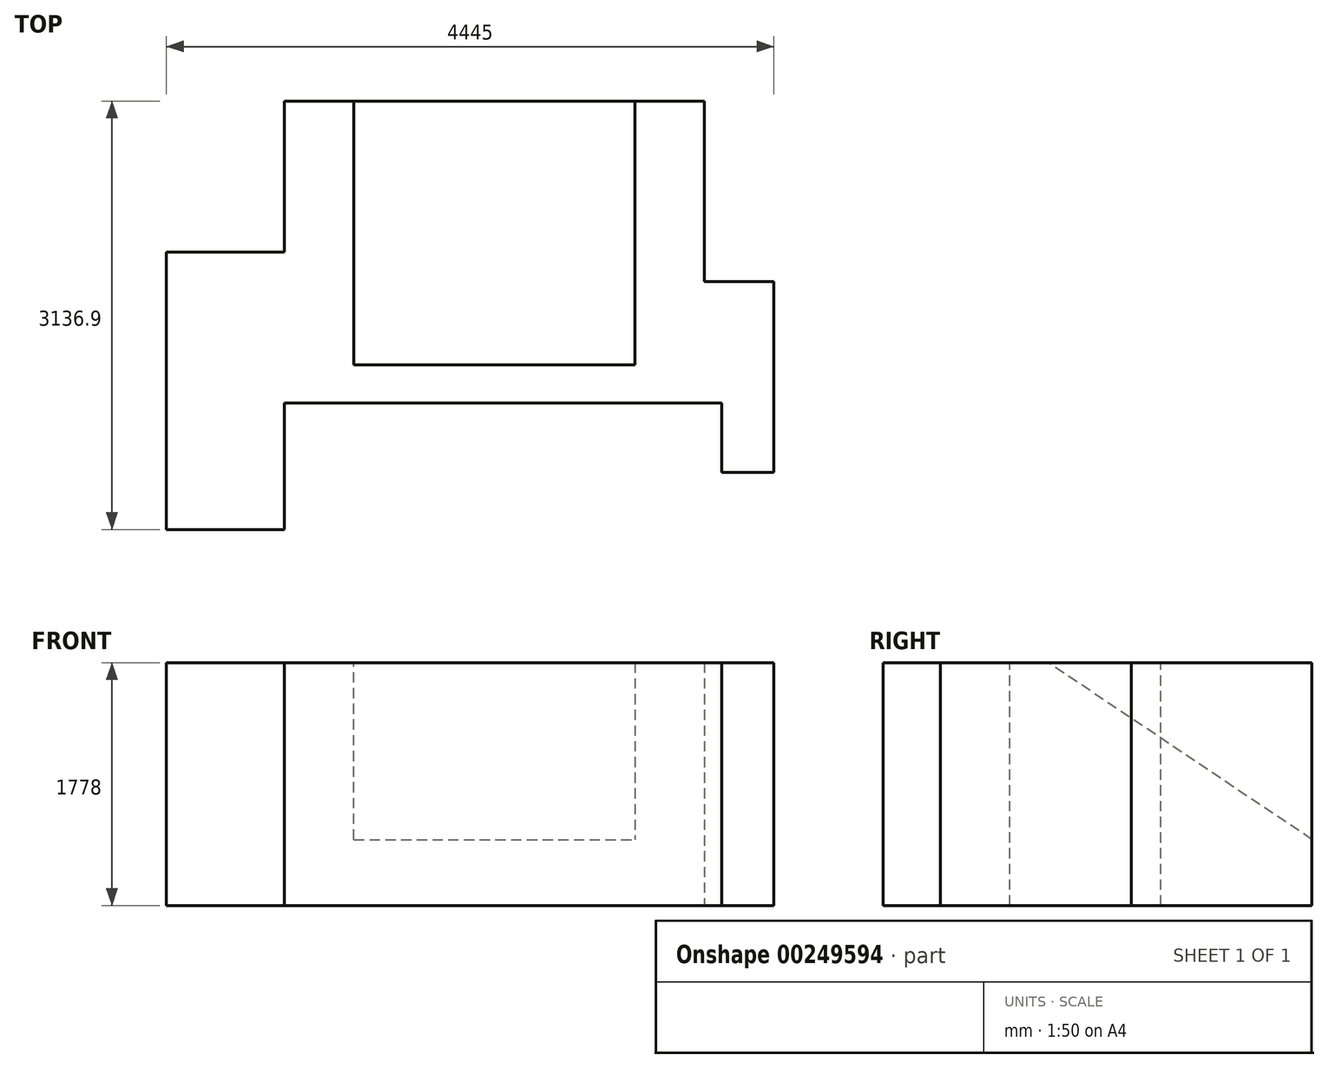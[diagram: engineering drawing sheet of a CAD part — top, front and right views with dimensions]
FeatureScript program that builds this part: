
annotation { "Feature Type Name" : "Feature", "Feature Type Description" : "" }
export const myFeature = defineFeature(function(context is Context, id is Id, definition is map)
    precondition{}
    {
        {
            var Q0;
            Q0=qCreatedBy(makeId("Top.planeOp"),FACE);
            var sketch = newSketch(context, id + "F0", { "sketchPlane" : qUnion([Q0])});
            skLineSegment(sketch, "E0.bottom", {"start": v(0, 0) * mm, "end": v(2057.4, 0) * mm});
            skLineSegment(sketch, "E0.top", {"start": v(0, 1930.4) * mm, "end": v(2057.4, 1930.4) * mm});
            skLineSegment(sketch, "E0.left", {"start": v(0, 0) * mm, "end": v(0, 1930.4) * mm});
            skLineSegment(sketch, "E0.right", {"start": v(2057.4, 0) * mm, "end": v(2057.4, 1930.4) * mm});
            skSolve(sketch);
        }
        {
            var Q0;
            Q0=makeQuery(id+"F0.imprint","IMPRINT",FACE,{"disambiguationData":[TD([[makeQuery(id+"F0.imprint","IMPRINT",EDGE,{"derivedFrom":sQuery(id+"F0.wireOp",EDGE,"E0.bottom")}),1.0]])]});
            extrude(context, id + "F1", {"entities" : qUnion([Q0]), "depth" : 1295.4 * mm});
        }
        {
            var Q0;
            Q0=makeQuery(id+"F1.opExtrude","CAP_EDGE",EDGE,{"disambiguationData":[OSD([sQuery(id+"F0.wireOp",EDGE,"E0.top")])],"isStart":false});
            chamfer(context, id + "F2", {"entities" : qUnion([Q0]), "chamferType" : ChamferType.TWO_OFFSETS, "width1" : 1295.4 * mm, "oppositeDirection" : false, "width2" : 1930.4 * mm, "tangentPropagation" : true});
        }
        {
            var Q0;
            Q0=makeQuery(id+"F1.opExtrude","SWEPT_FACE",FACE,{"disambiguationData":[OSD([sQuery(id+"F0.wireOp",EDGE,"E0.left")])]});
            var sketch = newSketch(context, id + "F3", { "sketchPlane" : qUnion([Q0])});
            skLineSegment(sketch, "E1.bottom", {"start": v(0, 0) * mm, "end": v(-1930.4, 0) * mm});
            skLineSegment(sketch, "E1.top", {"start": v(0, 1295.4) * mm, "end": v(-1930.4, 1295.4) * mm});
            skLineSegment(sketch, "E1.left", {"start": v(0, 0) * mm, "end": v(0, 1295.4) * mm});
            skLineSegment(sketch, "E1.right", {"start": v(-1930.4, 0) * mm, "end": v(-1930.4, 1295.4) * mm});
            skSolve(sketch);
        }
        {
            var Q0;
            Q0=makeQuery(id+"F3.imprint","IMPRINT",FACE,{"disambiguationData":[TD([[makeQuery(id+"F3.imprint","IMPRINT",EDGE,{"derivedFrom":sQuery(id+"F3.wireOp",EDGE,"E1.top")}),1.0]])]});
            var Q1;
            Q1=makeQuery(id+"F3.imprint","IMPRINT",FACE,{"disambiguationData":[TD([[makeQuery(id+"F3.imprint","IMPRINT",EDGE,{"derivedFrom":sQuery(id+"F3.wireOp",EDGE,"E1.bottom")}),-1.0]])]});
            extrude(context, id + "F4", {"entities" : qUnion([Q0, Q1]), "operationType" : NewBodyOperationType.ADD, "depth" : 508 * mm});
        }
        {
            var Q0;
            Q0=makeQuery(id+"F1.opExtrude","SWEPT_FACE",FACE,{"disambiguationData":[OSD([sQuery(id+"F0.wireOp",EDGE,"E0.right")])]});
            var sketch = newSketch(context, id + "F5", { "sketchPlane" : qUnion([Q0])});
            skLineSegment(sketch, "E2.0", {"start": v(0, 1295.4) * mm, "end": v(1930.4, 1295.4) * mm});
            skLineSegment(sketch, "E3.0", {"start": v(1930.4, 0) * mm, "end": v(1930.4, 1295.4) * mm});
            skLineSegment(sketch, "E4.top", {"start": v(0, 0) * mm, "end": v(1930.4, 0) * mm});
            skLineSegment(sketch, "E4.left", {"start": v(0, 1295.4) * mm, "end": v(0, 0) * mm});
            skLineSegment(sketch, "E4.right", {"start": v(1930.4, 1295.4) * mm, "end": v(1930.4, 0) * mm});
            skSolve(sketch);
        }
        {
            var Q0;
            Q0=makeQuery(id+"F5.imprint","IMPRINT",FACE,{"disambiguationData":[TD([[makeQuery(id+"F5.imprint","IMPRINT",EDGE,{"derivedFrom":sQuery(id+"F5.wireOp",EDGE,"E2.0")}),-1.0]])]});
            var Q1;
            Q1=makeQuery(id+"F5.imprint","IMPRINT",FACE,{"disambiguationData":[TD([[makeQuery(id+"F5.imprint","IMPRINT",EDGE,{"derivedFrom":sQuery(id+"F5.wireOp",EDGE,"E4.top")}),1.0]])]});
            extrude(context, id + "F6", {"entities" : qUnion([Q0, Q1]), "operationType" : NewBodyOperationType.ADD, "depth" : 508 * mm});
        }
        {
            var Q0;
            Q0=makeQuery(id+"F6.boolean.opBoolean","MERGE",FACE,{"derivedFrom":[makeQuery(id+"F4.boolean.opBoolean","MERGE",FACE,{"derivedFrom":[makeQuery(id+"F1.opExtrude","CAP_FACE",FACE,{"disambiguationData":[OSD([sQuery(id+"F0.wireOp",EDGE,"E0.bottom"),sQuery(id+"F0.wireOp",EDGE,"E0.top"),sQuery(id+"F0.wireOp",EDGE,"E0.left"),sQuery(id+"F0.wireOp",EDGE,"E0.right")])],"isStart":true}),makeQuery(id+"F4.opExtrude","SWEPT_FACE",FACE,{"disambiguationData":[OSD([sQuery(id+"F3.wireOp",EDGE,"E1.bottom")])]})]}),makeQuery(id+"F6.opExtrude","SWEPT_FACE",FACE,{"disambiguationData":[OSD([sQuery(id+"F5.wireOp",EDGE,"E4.top")])]})]});
            var sketch = newSketch(context, id + "F7", { "sketchPlane" : qUnion([Q0])});
            skLineSegment(sketch, "E5.bottom", {"start": v(-508, -1930.4) * mm, "end": v(2565.4, -1930.4) * mm});
            skLineSegment(sketch, "E5.top", {"start": v(-508, 0) * mm, "end": v(2565.4, 0) * mm});
            skLineSegment(sketch, "E5.left", {"start": v(-508, -1930.4) * mm, "end": v(-508, 0) * mm});
            skLineSegment(sketch, "E5.right", {"start": v(2565.4, -1930.4) * mm, "end": v(2565.4, 0) * mm});
            skSolve(sketch);
        }
        {
            var Q0;
            Q0=makeQuery(id+"F7.imprint","IMPRINT",FACE,{"disambiguationData":[TD([[makeQuery(id+"F7.imprint","IMPRINT",EDGE,{"derivedFrom":sQuery(id+"F7.wireOp",EDGE,"E5.top")}),-1.0]])]});
            extrude(context, id + "F8", {"entities" : qUnion([Q0]), "operationType" : NewBodyOperationType.ADD, "depth" : 482.6 * mm});
        }
        {
            var Q0;
            Q0=makeQuery(id+"F8.boolean.opBoolean","MERGE",FACE,{"derivedFrom":[makeQuery(id+"F6.boolean.opBoolean","MERGE",FACE,{"derivedFrom":[makeQuery(id+"F4.boolean.opBoolean","MERGE",FACE,{"derivedFrom":[makeQuery(id+"F1.opExtrude","SWEPT_FACE",FACE,{"disambiguationData":[OSD([sQuery(id+"F0.wireOp",EDGE,"E0.bottom")])]}),makeQuery(id+"F4.opExtrude","SWEPT_FACE",FACE,{"disambiguationData":[OSD([sQuery(id+"F3.wireOp",EDGE,"E1.left")])]})]}),makeQuery(id+"F6.opExtrude","SWEPT_FACE",FACE,{"disambiguationData":[OSD([sQuery(id+"F5.wireOp",EDGE,"E4.left")])]})]}),makeQuery(id+"F8.opExtrude","SWEPT_FACE",FACE,{"disambiguationData":[OSD([sQuery(id+"F7.wireOp",EDGE,"E5.top")])]})]});
            var sketch = newSketch(context, id + "F9", { "sketchPlane" : qUnion([Q0])});
            skLineSegment(sketch, "E6.bottom", {"start": v(-508, -482.6) * mm, "end": v(2565.4, -482.6) * mm});
            skLineSegment(sketch, "E6.top", {"start": v(-508, 1295.4) * mm, "end": v(2565.4, 1295.4) * mm});
            skLineSegment(sketch, "E6.left", {"start": v(-508, -482.6) * mm, "end": v(-508, 1295.4) * mm});
            skLineSegment(sketch, "E6.right", {"start": v(2565.4, -482.6) * mm, "end": v(2565.4, 1295.4) * mm});
            skSolve(sketch);
        }
        {
            var Q0;
            Q0=makeQuery(id+"F9.imprint","IMPRINT",FACE,{"disambiguationData":[TD([[makeQuery(id+"F9.imprint","IMPRINT",EDGE,{"derivedFrom":sQuery(id+"F9.wireOp",EDGE,"E6.bottom")}),1.0]])]});
            extrude(context, id + "F10", {"entities" : qUnion([Q0]), "operationType" : NewBodyOperationType.ADD, "depth" : 279.4 * mm});
        }
        {
            var Q0;
            Q0=makeQuery(id+"F10.boolean.opBoolean","MERGE",FACE,{"derivedFrom":[makeQuery(id+"F8.boolean.opBoolean","MERGE",FACE,{"derivedFrom":[makeQuery(id+"F4.opExtrude","CAP_FACE",FACE,{"disambiguationData":[OSD([sQuery(id+"F3.wireOp",EDGE,"E1.bottom"),sQuery(id+"F3.wireOp",EDGE,"E1.top"),sQuery(id+"F3.wireOp",EDGE,"E1.left"),sQuery(id+"F3.wireOp",EDGE,"E1.right")])],"isStart":false}),makeQuery(id+"F8.opExtrude","SWEPT_FACE",FACE,{"disambiguationData":[OSD([sQuery(id+"F7.wireOp",EDGE,"E5.left")])]})]}),makeQuery(id+"F10.opExtrude","SWEPT_FACE",FACE,{"disambiguationData":[OSD([sQuery(id+"F9.wireOp",EDGE,"E6.left")])]})]});
            var sketch = newSketch(context, id + "F11", { "sketchPlane" : qUnion([Q0])});
            skLineSegment(sketch, "E7.bottom", {"start": v(-1930.4, -482.6) * mm, "end": v(-825.5, -482.6) * mm});
            skLineSegment(sketch, "E7.top", {"start": v(-1930.4, 1295.4) * mm, "end": v(-825.5, 1295.4) * mm});
            skLineSegment(sketch, "E7.left", {"start": v(-1930.4, -482.6) * mm, "end": v(-1930.4, 1295.4) * mm});
            skLineSegment(sketch, "E7.right", {"start": v(-825.5, -482.6) * mm, "end": v(-825.5, 1295.4) * mm});
            skLineSegment(sketch, "E8.bottom", {"start": v(-825.5, -482.6) * mm, "end": v(1206.5, -482.6) * mm});
            skLineSegment(sketch, "E8.top", {"start": v(-825.5, 1295.4) * mm, "end": v(1206.5, 1295.4) * mm});
            skLineSegment(sketch, "E8.right", {"start": v(1206.5, -482.6) * mm, "end": v(1206.5, 1295.4) * mm});
            skSolve(sketch);
        }
        {
            var Q0;
            {var subQ2=sQuery(id+"F11.wireOp",EDGE,"E8.right");Q0=makeQuery(id+"F11.imprint","IMPRINT",FACE,{"disambiguationData":[TD([[makeQuery(id+"F11.imprint","IMPRINT",EDGE,{"derivedFrom":subQ2}),1.0]])]});}
            var Q1;
            {var subQ2=sQuery(id+"F11.wireOp",EDGE,"E7.right");Q1=makeQuery(id+"F11.imprint","IMPRINT",FACE,{"disambiguationData":[TD([[makeQuery(id+"F11.imprint","IMPRINT",EDGE,{"derivedFrom":subQ2}),-1.0]])]});}
            extrude(context, id + "F12", {"entities" : qUnion([Q0, Q1]), "operationType" : NewBodyOperationType.ADD, "depth" : 863.6 * mm});
        }
        {
            var Q0;
            Q0=makeQuery(id+"F10.boolean.opBoolean","MERGE",FACE,{"derivedFrom":[makeQuery(id+"F8.boolean.opBoolean","MERGE",FACE,{"derivedFrom":[makeQuery(id+"F6.opExtrude","CAP_FACE",FACE,{"disambiguationData":[OSD([sQuery(id+"F5.wireOp",EDGE,"E2.0"),sQuery(id+"F5.wireOp",EDGE,"E4.top"),sQuery(id+"F5.wireOp",EDGE,"E4.left"),sQuery(id+"F5.wireOp",EDGE,"E4.right")])],"isStart":false}),makeQuery(id+"F8.opExtrude","SWEPT_FACE",FACE,{"disambiguationData":[OSD([sQuery(id+"F7.wireOp",EDGE,"E5.right")])]})]}),makeQuery(id+"F10.opExtrude","SWEPT_FACE",FACE,{"disambiguationData":[OSD([sQuery(id+"F9.wireOp",EDGE,"E6.right")])]})]});
            var sketch = newSketch(context, id + "F13", { "sketchPlane" : qUnion([Q0])});
            skLineSegment(sketch, "E9.bottom", {"start": v(1930.4, 1295.4) * mm, "end": v(609.6, 1295.4) * mm});
            skLineSegment(sketch, "E9.top", {"start": v(1930.4, -482.6) * mm, "end": v(609.6, -482.6) * mm});
            skLineSegment(sketch, "E9.left", {"start": v(1930.4, 1295.4) * mm, "end": v(1930.4, -482.6) * mm});
            skLineSegment(sketch, "E9.right", {"start": v(609.6, 1295.4) * mm, "end": v(609.6, -482.6) * mm});
            skLineSegment(sketch, "E10.bottom", {"start": v(609.6, -482.6) * mm, "end": v(-279.4, -482.6) * mm});
            skLineSegment(sketch, "E10.top", {"start": v(609.6, 1295.4) * mm, "end": v(-279.4, 1295.4) * mm});
            skLineSegment(sketch, "E10.left", {"start": v(609.6, -482.6) * mm, "end": v(609.6, 1295.4) * mm});
            skLineSegment(sketch, "E10.right", {"start": v(-279.4, -482.6) * mm, "end": v(-279.4, 1295.4) * mm});
            skSolve(sketch);
        }
        {
            var Q0;
            Q0=makeQuery(id+"F13.imprint","IMPRINT",FACE,{"disambiguationData":[TD([[makeQuery(id+"F13.imprint","IMPRINT",EDGE,{"derivedFrom":sQuery(id+"F13.wireOp",EDGE,"E10.bottom")}),1.0]])]});
            extrude(context, id + "F14", {"entities" : qUnion([Q0]), "operationType" : NewBodyOperationType.ADD, "depth" : 508 * mm});
        }
        {
            var Q0;
            Q0=makeQuery(id+"F14.boolean.opBoolean","MERGE",FACE,{"derivedFrom":[makeQuery(id+"F10.opExtrude","CAP_FACE",FACE,{"disambiguationData":[OSD([sQuery(id+"F9.wireOp",EDGE,"E6.bottom"),sQuery(id+"F9.wireOp",EDGE,"E6.top"),sQuery(id+"F9.wireOp",EDGE,"E6.left"),sQuery(id+"F9.wireOp",EDGE,"E6.right")])],"isStart":false}),makeQuery(id+"F14.opExtrude","SWEPT_FACE",FACE,{"disambiguationData":[OSD([sQuery(id+"F13.wireOp",EDGE,"E10.right")])]})]});
            var sketch = newSketch(context, id + "F15", { "sketchPlane" : qUnion([Q0])});
            skLineSegment(sketch, "E11.bottom", {"start": v(3073.4, -482.6) * mm, "end": v(2692.4, -482.6) * mm});
            skLineSegment(sketch, "E11.top", {"start": v(3073.4, 1295.4) * mm, "end": v(2692.4, 1295.4) * mm});
            skLineSegment(sketch, "E11.left", {"start": v(3073.4, -482.6) * mm, "end": v(3073.4, 1295.4) * mm});
            skLineSegment(sketch, "E11.right", {"start": v(2692.4, -482.6) * mm, "end": v(2692.4, 1295.4) * mm});
            skSolve(sketch);
        }
        {
            var Q0;
            Q0=makeQuery(id+"F15.imprint","IMPRINT",FACE,{"disambiguationData":[TD([[makeQuery(id+"F15.imprint","IMPRINT",EDGE,{"derivedFrom":sQuery(id+"F15.wireOp",EDGE,"E11.bottom")}),1.0]])]});
            extrude(context, id + "F16", {"entities" : qUnion([Q0]), "operationType" : NewBodyOperationType.ADD, "depth" : 508 * mm});
        }
    });
